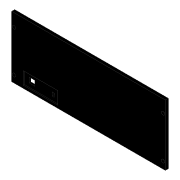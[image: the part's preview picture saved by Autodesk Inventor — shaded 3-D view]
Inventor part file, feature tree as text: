
AUTODESK INVENTOR PART (.ipt)
format: ipt  version: 2020 (Build 240168000, 168)  size: 185,344 bytes
history: native  units: mm
features: extrude x4, sketch x4
ambient origin geometry x8: Origin, YZ Plane, XZ Plane, XY Plane, X Axis, Y Axis, Z Axis, Center Point
bodies: Solid1 (feature_tree)
feature tree (8):
  extrude  "Extrusion1"  Depth=4.5mm
  extrude  "Extrusion2"  Depth=4.5mm
  extrude  "Extrusion3"  Depth=6.5mm TaperAngle=0.0deg
  extrude  "Extrusion4"  Depth=2.5mm
  sketch  "Sketch1"  dims[d0=330.0mm d1=4.5mm]
  sketch  "Sketch2"  dims[d2=4.5mm d3=4.5mm]
  sketch  "Sketch3"  dims[d4=4.5mm d5=6.5mm d6=0.0mm]
  sketch  "Sketch4"  dims[d7=7.1mm d8=7.1mm d9=7.1mm d10=7.1mm d11=4.5mm d12=0.0mm d13=14.15mm d14=282.73mm d36=20.1mm d37=10.16mm d38=10.16mm d39=12.032239mm d40=11.12mm d41=10.5mm d44=8.0mm d45=0.46mm d46=0.46mm d47=0.5mm d48=0.5mm d51=9.003283mm d52=0.5mm d53=0.499974mm d54=0.498469mm d55=0.499752mm d57=0.0mm d58=0.0mm d59=0.2mm d60=9.0mm d61=11.0mm d62=0.5mm d63=0.2mm d64=4.5mm d65=7.75mm d66=8.0mm d67=0.0mm d68=0.0mm d69=10.0mm d70=10.0mm d71=8.0mm d72=8.0mm d73=2.5mm d74=0.0mm]
